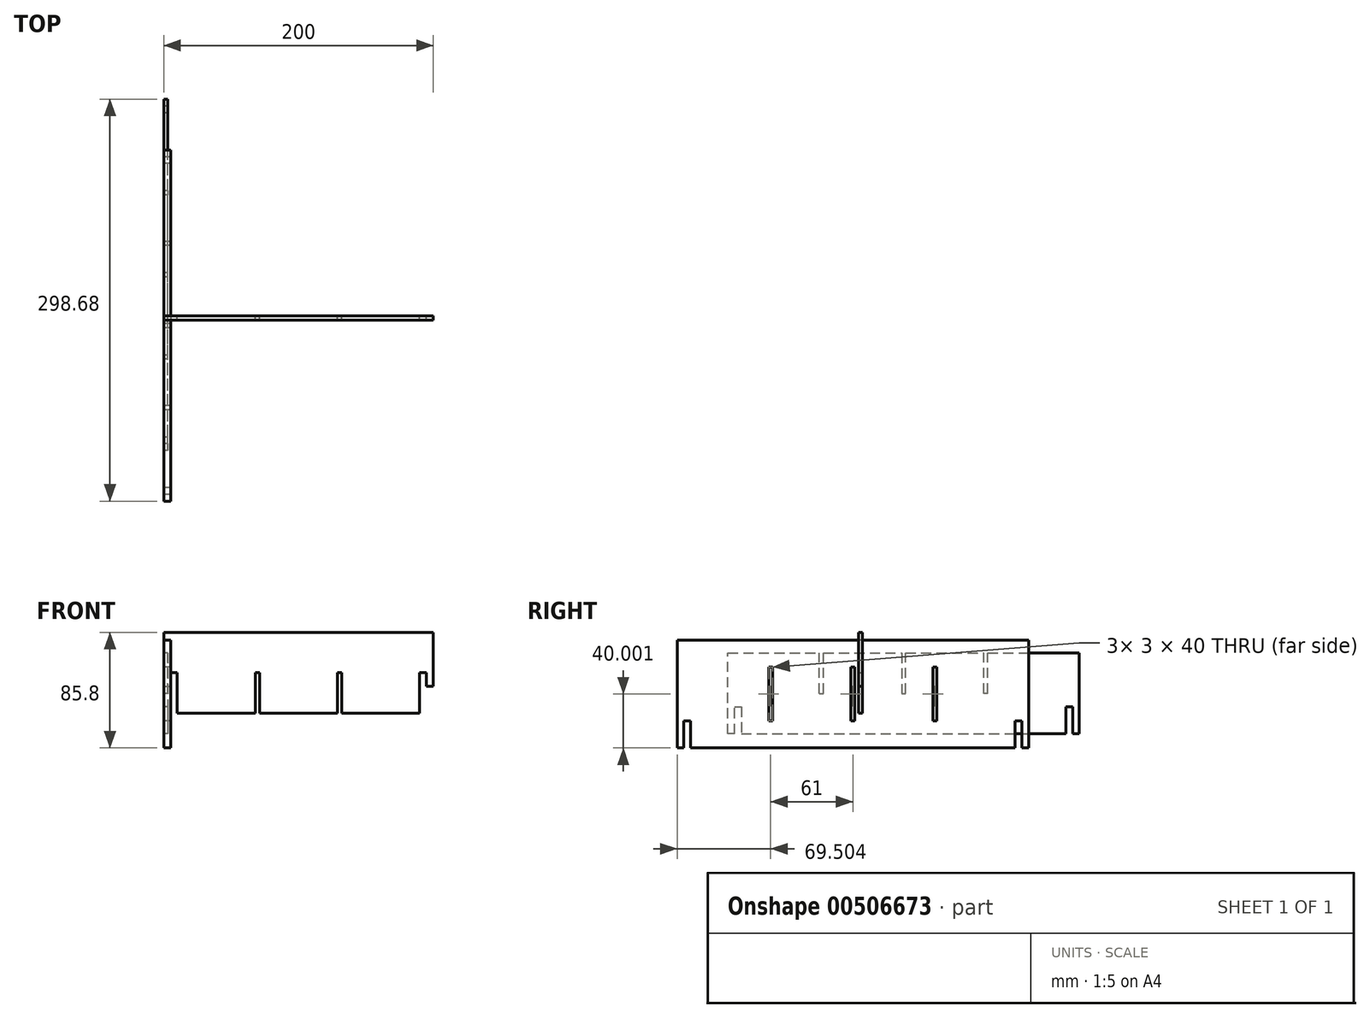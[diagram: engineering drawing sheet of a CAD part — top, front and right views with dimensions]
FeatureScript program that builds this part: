
annotation { "Feature Type Name" : "Feature", "Feature Type Description" : "" }
export const myFeature = defineFeature(function(context is Context, id is Id, definition is map)
    precondition{}
    {
        {
            var Q0;
            Q0=qCreatedBy(makeId("Front.planeOp"),FACE);
            var sketch = newSketch(context, id + "F0", { "sketchPlane" : qUnion([Q0])});
            skLineSegment(sketch, "E0", {"start": v(0, 20) * mm, "end": v(0, 60) * mm});
            skLineSegment(sketch, "E1", {"start": v(0, 60) * mm, "end": v(200, 60) * mm});
            skLineSegment(sketch, "E2", {"start": v(100, 60) * mm, "end": v(100, -25.65) * mm, "construction": true});
            skPoint(sketch, "E2.endSnap0", {"position": v(100, 0) * mm});
            skLineSegment(sketch, "E3", {"start": v(5, 30) * mm, "end": v(10, 30) * mm});
            skLineSegment(sketch, "E4", {"start": v(10, 30) * mm, "end": v(10, 0) * mm});
            skLineSegment(sketch, "E5.MirrorCS", {"start": v(190, 30) * mm, "end": v(190, 0) * mm});
            skLineSegment(sketch, "E6.MirrorCS", {"start": v(195, 30) * mm, "end": v(190, 30) * mm});
            skLineSegment(sketch, "E7.trimOffspring", {"start": v(190, 0) * mm, "end": v(132, 0) * mm});
            skLineSegment(sketch, "E8", {"start": v(68, 0) * mm, "end": v(68, 30) * mm});
            skLineSegment(sketch, "E9", {"start": v(68, 30) * mm, "end": v(71, 30) * mm});
            skLineSegment(sketch, "E10", {"start": v(71, 30) * mm, "end": v(71, 0) * mm});
            skLineSegment(sketch, "E11.trimOffspring", {"start": v(68, 0) * mm, "end": v(10, 0) * mm});
            skLineSegment(sketch, "E12.MirrorCS", {"start": v(129, 30) * mm, "end": v(129, 0) * mm});
            skLineSegment(sketch, "E13.MirrorCS", {"start": v(132, 30) * mm, "end": v(129, 30) * mm});
            skLineSegment(sketch, "E14.MirrorCS", {"start": v(132, 0) * mm, "end": v(132, 30) * mm});
            skLineSegment(sketch, "E15.trimOffspring", {"start": v(129, 0) * mm, "end": v(71, 0) * mm});
            skLineSegment(sketch, "E16", {"start": v(0, 20) * mm, "end": v(5, 20) * mm});
            skLineSegment(sketch, "E17", {"start": v(5, 20) * mm, "end": v(5, 30) * mm});
            skLineSegment(sketch, "E18.MirrorCS", {"start": v(195, 20) * mm, "end": v(195, 30) * mm});
            skLineSegment(sketch, "E19.MirrorCS", {"start": v(200, 20) * mm, "end": v(200, 60) * mm});
            skLineSegment(sketch, "E20.MirrorCS", {"start": v(200, 20) * mm, "end": v(195, 20) * mm});
            skSolve(sketch);
        }
        {
            var Q0;
            Q0 = qSketchRegion(id + "F0", true);
            extrude(context, id + "F1", {"entities" : qUnion([Q0]), "depth" : 3 * mm});
        }
        {
            var Q0;
            Q0=qCreatedBy(makeId("Right.planeOp"),FACE);
            var sketch = newSketch(context, id + "F2", { "sketchPlane" : qUnion([Q0])});
            skLineSegment(sketch, "E21", {"start": v(-100, -15.33) * mm, "end": v(-100, 44.67) * mm});
            skLineSegment(sketch, "E22", {"start": v(-100, 44.67) * mm, "end": v(-32, 44.67) * mm});
            skLineSegment(sketch, "E23", {"start": v(161, 44.67) * mm, "end": v(161, -15.33) * mm});
            skLineSegment(sketch, "E24", {"start": v(161, -15.33) * mm, "end": v(156, -15.33) * mm});
            skLineSegment(sketch, "E25", {"start": v(30.5, 44.67) * mm, "end": v(30.5, -40.97) * mm, "construction": true});
            skPoint(sketch, "E25.endSnap0", {"position": v(30.5, -15.33) * mm});
            skLineSegment(sketch, "E26", {"start": v(-95, -15.33) * mm, "end": v(-95, 4.67) * mm});
            skLineSegment(sketch, "E27", {"start": v(-95, 4.67) * mm, "end": v(-90, 4.67) * mm});
            skLineSegment(sketch, "E28", {"start": v(-90, 4.67) * mm, "end": v(-90, -15.33) * mm});
            skLineSegment(sketch, "E29.trimOffspring", {"start": v(-95, -15.33) * mm, "end": v(-100, -15.33) * mm});
            skLineSegment(sketch, "E30.MirrorCS", {"start": v(151, 4.67) * mm, "end": v(151, -15.33) * mm});
            skLineSegment(sketch, "E31.MirrorCS", {"start": v(156, -15.33) * mm, "end": v(156, 4.67) * mm});
            skLineSegment(sketch, "E32.MirrorCS", {"start": v(156, 4.67) * mm, "end": v(151, 4.67) * mm});
            skLineSegment(sketch, "E33", {"start": v(-32, 14.67) * mm, "end": v(-29, 14.67) * mm});
            skLineSegment(sketch, "E34", {"start": v(-32, 14.67) * mm, "end": v(-32, 44.67) * mm});
            skLineSegment(sketch, "E35", {"start": v(-29, 14.67) * mm, "end": v(-29, 44.67) * mm});
            skLineSegment(sketch, "E36.trimOffspring", {"start": v(-29, 44.67) * mm, "end": v(29, 44.67) * mm});
            skPoint(sketch, "E37.MirrorCS.end.orphan", {"position": v(93, 14.67) * mm});
            skPoint(sketch, "E38.MirrorCS.end.orphan", {"position": v(90, 14.67) * mm});
            skLineSegment(sketch, "E39.MirrorCS", {"start": v(90, 14.67) * mm, "end": v(90, 44.67) * mm});
            skLineSegment(sketch, "E40.MirrorCS", {"start": v(93, 14.67) * mm, "end": v(93, 44.67) * mm});
            skLineSegment(sketch, "E41.MirrorCS", {"start": v(93, 14.67) * mm, "end": v(90, 14.67) * mm});
            skLineSegment(sketch, "E42.trimOffspring", {"start": v(93, 44.67) * mm, "end": v(161, 44.67) * mm});
            skPoint(sketch, "E43.start.orphan", {"position": v(29, -15.33) * mm});
            skPoint(sketch, "E44.trimOffspring.start.orphan", {"position": v(32, -15.33) * mm});
            skPoint(sketch, "E45.trimOffspring.end.orphan", {"position": v(93, -15.33) * mm});
            skPoint(sketch, "E46.trimOffspring.start.orphan", {"position": v(-32, -15.33) * mm});
            skLineSegment(sketch, "E47", {"start": v(-90, -15.33) * mm, "end": v(151, -15.33) * mm});
            skLineSegment(sketch, "E48", {"start": v(29, 44.67) * mm, "end": v(29, 14.67) * mm});
            skLineSegment(sketch, "E49", {"start": v(29, 14.67) * mm, "end": v(32, 14.67) * mm});
            skLineSegment(sketch, "E50", {"start": v(32, 14.67) * mm, "end": v(32, 44.67) * mm});
            skLineSegment(sketch, "E51.trimOffspring", {"start": v(32, 44.67) * mm, "end": v(90, 44.67) * mm});
            skSolve(sketch);
        }
        {
            var Q0;
            Q0 = qSketchRegion(id + "F2", true);
            extrude(context, id + "F3", {"entities" : qUnion([Q0]), "depth" : 3 * mm});
        }
        {
            var Q0;
            Q0=qCreatedBy(makeId("Right.planeOp"),FACE);
            var sketch = newSketch(context, id + "F4", { "sketchPlane" : qUnion([Q0])});
            skLineSegment(sketch, "E52", {"start": v(123.32, -25.8) * mm, "end": v(118.32, -25.8) * mm});
            skLineSegment(sketch, "E53", {"start": v(-7.18, 34.22) * mm, "end": v(-7.18, -51.42) * mm, "construction": true});
            skPoint(sketch, "E53.endSnap0", {"position": v(-7.18, -25.8) * mm});
            skLineSegment(sketch, "E54", {"start": v(-132.68, -25.8) * mm, "end": v(-132.68, -5.8) * mm});
            skLineSegment(sketch, "E55", {"start": v(-132.68, -5.8) * mm, "end": v(-127.68, -5.8) * mm});
            skLineSegment(sketch, "E56", {"start": v(-127.68, -5.8) * mm, "end": v(-127.68, -25.8) * mm});
            skLineSegment(sketch, "E57.trimOffspring", {"start": v(-132.68, -25.8) * mm, "end": v(-137.68, -25.8) * mm});
            skLineSegment(sketch, "E58.MirrorCS", {"start": v(113.32, -5.8) * mm, "end": v(113.32, -25.8) * mm});
            skLineSegment(sketch, "E59.MirrorCS", {"start": v(118.32, -25.8) * mm, "end": v(118.32, -5.8) * mm});
            skLineSegment(sketch, "E60.MirrorCS", {"start": v(118.32, -5.8) * mm, "end": v(113.32, -5.8) * mm});
            skLineSegment(sketch, "E61", {"start": v(-69.68, -5.8) * mm, "end": v(-66.68, -5.8) * mm});
            skLineSegment(sketch, "E62", {"start": v(-69.68, -5.8) * mm, "end": v(-69.68, 34.2) * mm});
            skLineSegment(sketch, "E63", {"start": v(-66.68, -5.8) * mm, "end": v(-66.68, 34.2) * mm});
            skPoint(sketch, "E64.MirrorCS.end.orphan", {"position": v(55.32, -5.8) * mm});
            skPoint(sketch, "E65.MirrorCS.end.orphan", {"position": v(52.32, -5.8) * mm});
            skLineSegment(sketch, "E66.MirrorCS", {"start": v(52.32, -5.8) * mm, "end": v(52.32, 34.2) * mm});
            skLineSegment(sketch, "E67.MirrorCS", {"start": v(55.32, -5.8) * mm, "end": v(55.32, 34.2) * mm});
            skLineSegment(sketch, "E68.MirrorCS", {"start": v(55.32, -5.8) * mm, "end": v(52.32, -5.8) * mm});
            skPoint(sketch, "E69.start.orphan", {"position": v(-8.68, -25.8) * mm});
            skPoint(sketch, "E70.trimOffspring.start.orphan", {"position": v(-5.68, -25.8) * mm});
            skPoint(sketch, "E71.trimOffspring.end.orphan", {"position": v(55.32, -25.8) * mm});
            skPoint(sketch, "E72.trimOffspring.start.orphan", {"position": v(-69.68, -25.8) * mm});
            skLineSegment(sketch, "E73", {"start": v(-127.68, -25.8) * mm, "end": v(113.32, -25.8) * mm});
            skLineSegment(sketch, "E74", {"start": v(-8.68, 34.2) * mm, "end": v(-8.68, -5.8) * mm});
            skLineSegment(sketch, "E75", {"start": v(-8.68, -5.8) * mm, "end": v(-5.68, -5.8) * mm});
            skLineSegment(sketch, "E76", {"start": v(-5.68, -5.8) * mm, "end": v(-5.68, 34.2) * mm});
            skLineSegment(sketch, "E77", {"start": v(123.32, 54.2) * mm, "end": v(-137.68, 54.2) * mm});
            skLineSegment(sketch, "E78", {"start": v(55.32, 34.2) * mm, "end": v(52.32, 34.2) * mm});
            skLineSegment(sketch, "E79", {"start": v(-5.68, 34.2) * mm, "end": v(-8.68, 34.2) * mm});
            skLineSegment(sketch, "E80", {"start": v(-66.68, 34.2) * mm, "end": v(-69.68, 34.2) * mm});
            skLineSegment(sketch, "E81", {"start": v(123.32, -25.8) * mm, "end": v(123.32, 54.2) * mm});
            skLineSegment(sketch, "E82", {"start": v(-137.68, -25.8) * mm, "end": v(-137.68, 54.2) * mm});
            skSolve(sketch);
        }
        {
            var Q0;
            Q0 = qSketchRegion(id + "F4", true);
            extrude(context, id + "F5", {"entities" : qUnion([Q0]), "depth" : 5 * mm, "offsetDistance" : 25 * mm});
        }
    });
